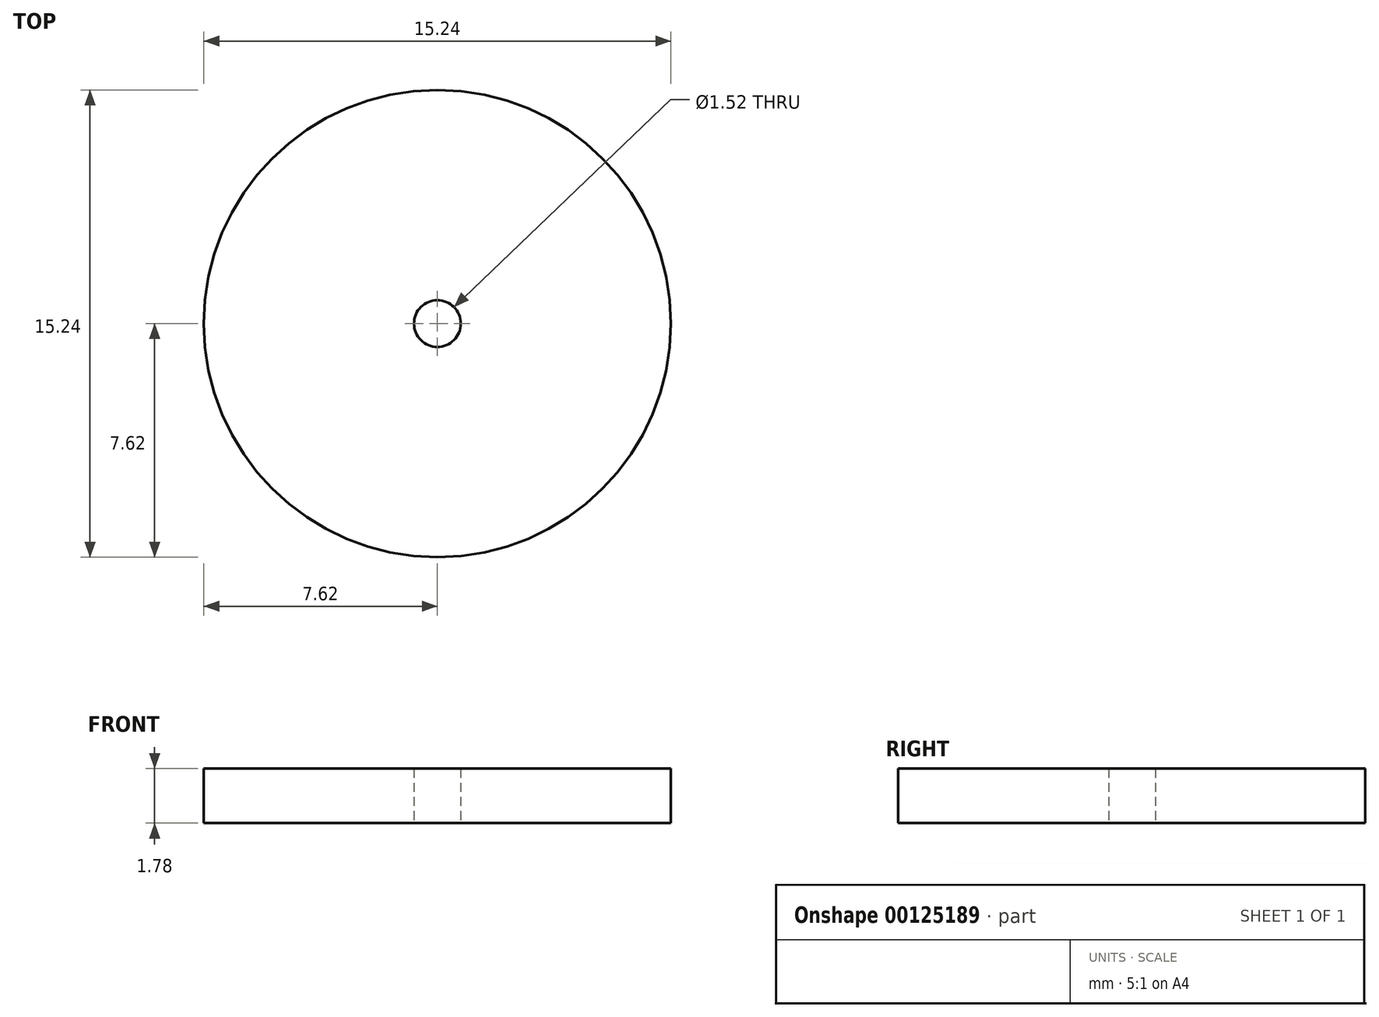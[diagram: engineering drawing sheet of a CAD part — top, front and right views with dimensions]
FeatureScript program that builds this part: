
annotation { "Feature Type Name" : "Feature", "Feature Type Description" : "" }
export const myFeature = defineFeature(function(context is Context, id is Id, definition is map)
    precondition{}
    {
        {
            var Q0;
            Q0=qCreatedBy(makeId("Top.planeOp"),FACE);
            var sketch = newSketch(context, id + "F0", { "sketchPlane" : qUnion([Q0])});
            skCircle(sketch, "E0", {"center": v(0, 0) * mm, "radius": 7.62 * mm});
            skCircle(sketch, "E1", {"center": v(0, 0) * mm, "radius": 0.76 * mm});
            skSolve(sketch);
        }
        {
            var Q0;
            Q0 = qSketchRegion(id + "F0", true);
            extrude(context, id + "F1", {"entities" : qUnion([Q0]), "depth" : 1.78 * mm});
        }
    });
